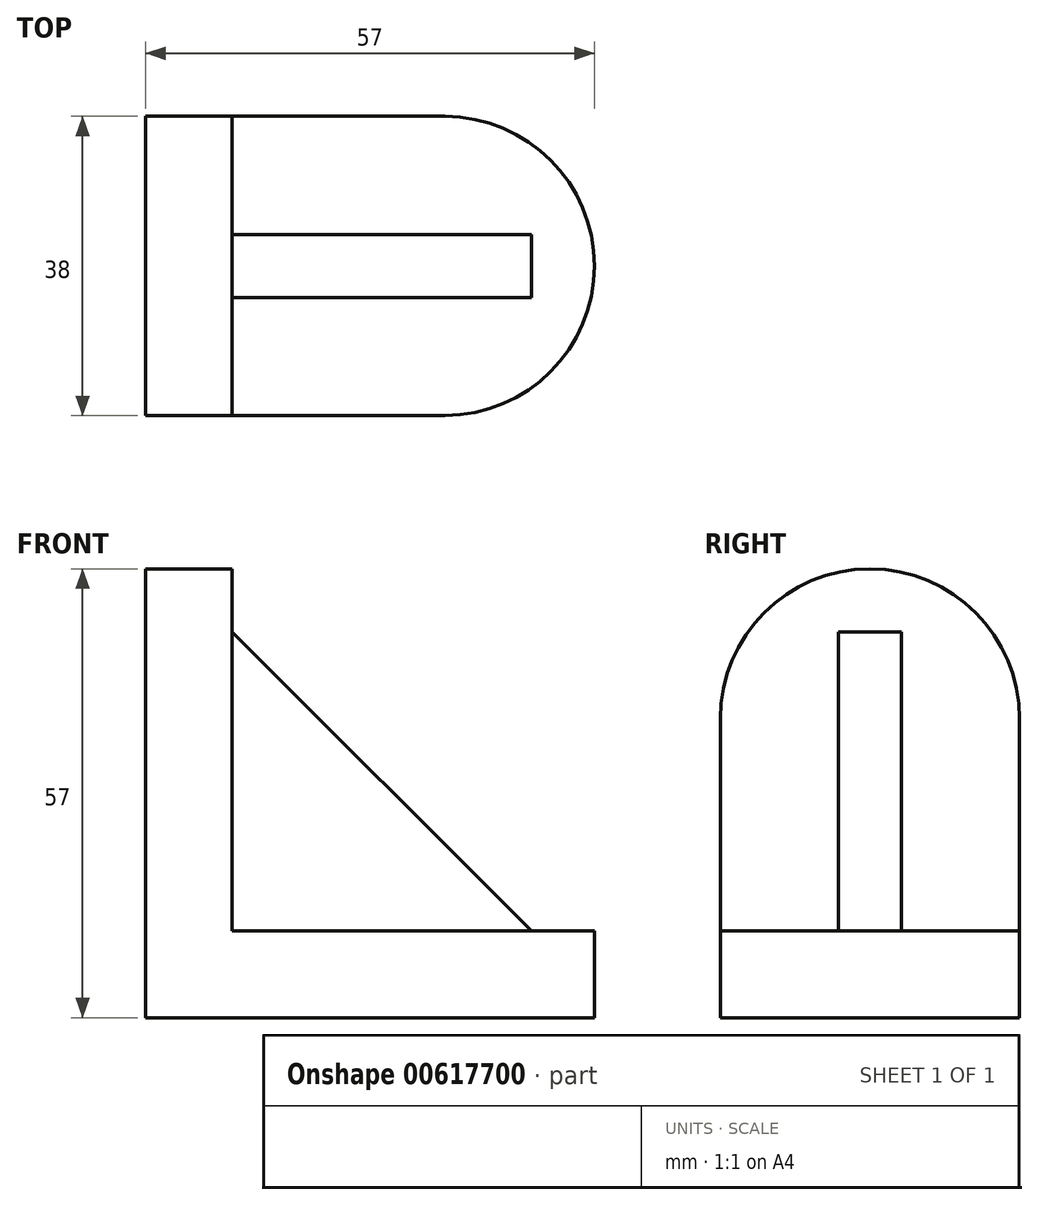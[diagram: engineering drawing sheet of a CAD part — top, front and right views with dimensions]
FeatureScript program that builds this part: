
annotation { "Feature Type Name" : "Feature", "Feature Type Description" : "" }
export const myFeature = defineFeature(function(context is Context, id is Id, definition is map)
    precondition{}
    {
        {
            var Q0;
            Q0=qCreatedBy(makeId("Right.planeOp"),FACE);
            var sketch = newSketch(context, id + "F0", { "sketchPlane" : qUnion([Q0])});
            skLineSegment(sketch, "E0.bottom", {"start": v(0, 0) * mm, "end": v(-38, 0) * mm});
            skLineSegment(sketch, "E0.top", {"start": v(-19, 57) * mm, "end": v(-19, 57) * mm});
            skLineSegment(sketch, "E0.left", {"start": v(0, 0) * mm, "end": v(0, 38) * mm});
            skLineSegment(sketch, "E0.right", {"start": v(-38, 0) * mm, "end": v(-38, 38) * mm});
            skPoint(sketch, "E1.visualSharp", {"position": v(-38, 57) * mm});
            skArc(sketch, "E1.filletArc", {"start": v(-19, 57) * mm, "mid": v(-32.44, 51.44) * mm, "end": v(-38, 38) * mm});
            skPoint(sketch, "E2.visualSharp", {"position": v(0, 57) * mm});
            skArc(sketch, "E2.filletArc", {"start": v(0, 38) * mm, "mid": v(-5.56, 51.44) * mm, "end": v(-19, 57) * mm});
            skSolve(sketch);
        }
        {
            var Q0;
            Q0=makeQuery(id+"F0.imprint","IMPRINT",FACE,{"disambiguationData":[TD([[makeQuery(id+"F0.imprint","IMPRINT",EDGE,{"derivedFrom":sQuery(id+"F0.wireOp",EDGE,"E0.bottom")}),-1.0]])]});
            extrude(context, id + "F1", {"entities" : qUnion([Q0]), "depth" : 11 * mm, "offsetDistance" : 25.4 * mm});
        }
        {
            var Q0;
            Q0=qCreatedBy(makeId("Top.planeOp"),FACE);
            var sketch = newSketch(context, id + "F2", { "sketchPlane" : qUnion([Q0])});
            skLineSegment(sketch, "E3.bottom", {"start": v(0, 0) * mm, "end": v(38, 0) * mm});
            skLineSegment(sketch, "E3.top", {"start": v(0, -38) * mm, "end": v(38, -38) * mm});
            skLineSegment(sketch, "E3.left", {"start": v(0, 0) * mm, "end": v(0, -38) * mm});
            skLineSegment(sketch, "E3.right", {"start": v(57, -19) * mm, "end": v(57, -19) * mm});
            skPoint(sketch, "E4.visualSharp", {"position": v(57, -38) * mm});
            skArc(sketch, "E4.filletArc", {"start": v(38, -38) * mm, "mid": v(51.44, -32.44) * mm, "end": v(57, -19) * mm});
            skPoint(sketch, "E5.visualSharp", {"position": v(57, 0) * mm});
            skArc(sketch, "E5.filletArc", {"start": v(57, -19) * mm, "mid": v(51.44, -5.56) * mm, "end": v(38, 0) * mm});
            skSolve(sketch);
        }
        {
            var Q0;
            Q0=makeQuery(id+"F2.imprint","IMPRINT",FACE,{"disambiguationData":[TD([[makeQuery(id+"F2.imprint","IMPRINT",EDGE,{"derivedFrom":sQuery(id+"F2.wireOp",EDGE,"E3.bottom")}),-1.0]])]});
            extrude(context, id + "F3", {"entities" : qUnion([Q0]), "operationType" : NewBodyOperationType.ADD, "depth" : 11 * mm, "offsetDistance" : 25.4 * mm});
        }
        {
            var Q0;
            Q0=makeQuery(id+"F3.boolean.opBoolean","INTERSECT",EDGE,{"derivedFrom":[makeQuery(id+"F1.opExtrude","CAP_FACE",FACE,{"disambiguationData":[OSD([sQuery(id+"F0.wireOp",EDGE,"E0.bottom"),sQuery(id+"F0.wireOp",EDGE,"E0.left"),sQuery(id+"F0.wireOp",EDGE,"E0.right"),sQuery(id+"F0.wireOp",EDGE,"E1.filletArc"),sQuery(id+"F0.wireOp",EDGE,"E2.filletArc")])],"isStart":false}),makeQuery(id+"F3.opExtrude","CAP_FACE",FACE,{"disambiguationData":[OSD([sQuery(id+"F2.wireOp",EDGE,"E3.bottom"),sQuery(id+"F2.wireOp",EDGE,"E3.top"),sQuery(id+"F2.wireOp",EDGE,"E3.left"),sQuery(id+"F2.wireOp",EDGE,"E4.filletArc"),sQuery(id+"F2.wireOp",EDGE,"E5.filletArc")])],"isStart":false})]});
            cPoint(context, id + "F4", {"entities" : qUnion([Q0]), "parameter" : 0.5});
        }
        {
            var Q0;
            Q0=makeQuery(id+"F3.opExtrude","CAP_EDGE",EDGE,{"disambiguationData":[OSD([sQuery(id+"F2.wireOp",EDGE,"E4.filletArc"),sQuery(id+"F2.wireOp",EDGE,"E5.filletArc")])],"isStart":false});
            cPoint(context, id + "F5", {"entities" : qUnion([Q0]), "parameter" : 0.5});
        }
        {
            var Q0;
            Q0=makeQuery(id+"F1.opExtrude","CAP_EDGE",EDGE,{"disambiguationData":[OSD([sQuery(id+"F0.wireOp",EDGE,"E1.filletArc"),sQuery(id+"F0.wireOp",EDGE,"E2.filletArc")])],"isStart":false});
            cPoint(context, id + "F6", {"entities" : qUnion([Q0]), "parameter" : 0.5});
        }
        {
            var Q0;
            Q0=qCreatedBy(id+"F4",VERTEX);
            var Q1;
            Q1=qCreatedBy(id+"F5",VERTEX);
            var Q2;
            Q2=qCreatedBy(id+"F6",VERTEX);
            cPlane(context, id + "F7", {"entities" : qUnion([Q0, Q1, Q2]), "cplaneType" : CPlaneType.THREE_POINT, "offset" : 25.4 * mm, "width" : 152.4 * mm, "height" : 152.4 * mm});
        }
        {
            var Q0;
            Q0=qCreatedBy(id+"F7.planeOp",FACE);
            var sketch = newSketch(context, id + "F8", { "sketchPlane" : qUnion([Q0])});
            skLineSegment(sketch, "E6", {"start": v(0, 0) * mm, "end": v(-49, 0) * mm});
            skLineSegment(sketch, "E7", {"start": v(-49, 0) * mm, "end": v(-49, 11) * mm});
            skLineSegment(sketch, "E8", {"start": v(-49, 11) * mm, "end": v(-11, 11) * mm});
            skLineSegment(sketch, "E9", {"start": v(-11, 11) * mm, "end": v(-11, 49) * mm});
            skLineSegment(sketch, "E10", {"start": v(-11, 49) * mm, "end": v(0, 49) * mm});
            skLineSegment(sketch, "E11", {"start": v(0, 49) * mm, "end": v(0, 0) * mm});
            skLineSegment(sketch, "E12", {"start": v(-11, 49) * mm, "end": v(-49, 11) * mm});
            skSolve(sketch);
        }
        {
            var Q0;
            Q0=makeQuery(id+"F8.imprint","IMPRINT",FACE,{"disambiguationData":[TD([[makeQuery(id+"F8.imprint","IMPRINT",EDGE,{"derivedFrom":sQuery(id+"F8.wireOp",EDGE,"E8")}),1.0]])]});
            extrude(context, id + "F9", {"entities" : qUnion([Q0]), "operationType" : NewBodyOperationType.ADD, "endBound" : BoundingType.SYMMETRIC, "depth" : 8 * mm, "offsetDistance" : 25.4 * mm});
        }
    });
